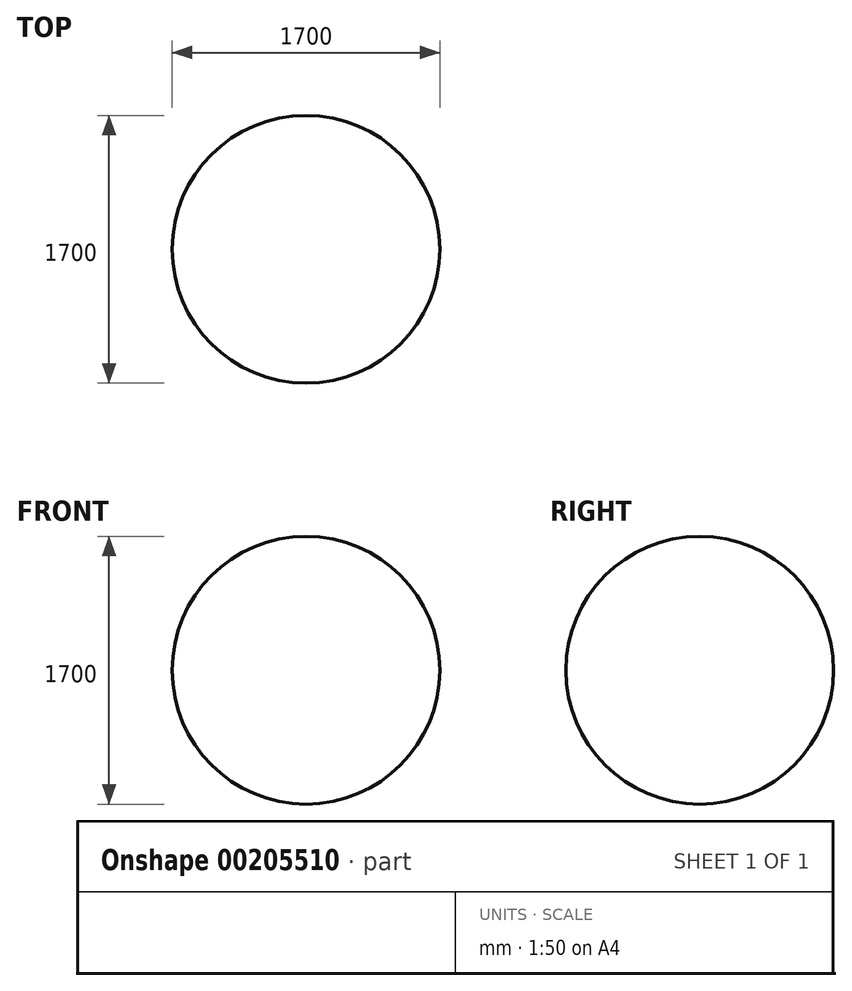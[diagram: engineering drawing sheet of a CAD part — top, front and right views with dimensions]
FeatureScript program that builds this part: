
annotation { "Feature Type Name" : "Feature", "Feature Type Description" : "" }
export const myFeature = defineFeature(function(context is Context, id is Id, definition is map)
    precondition{}
    {
        {
            var Q0;
            Q0=qCreatedBy(makeId("Front.planeOp"),FACE);
            var sketch = newSketch(context, id + "F0", { "sketchPlane" : qUnion([Q0])});
            skLineSegment(sketch, "E0", {"start": v(0, 0) * mm, "end": v(0, 850) * mm});
            skLineSegment(sketch, "E1", {"start": v(0, 0) * mm, "end": v(0, -850) * mm});
            skArc(sketch, "E2", {"start": v(0, 850) * mm, "mid": v(850, 0) * mm, "end": v(0, -850) * mm});
            skSolve(sketch);
        }
        {
            var Q0;
            Q0 = qSketchRegion(id + "F0", true);
            var Q1;
            Q1=sQuery(id+"F0.wireOp",EDGE,"E0");
            revolve(context, id + "F1", {"entities" : qUnion([Q0]), "axis" : qUnion([Q1]), "revolveType" : RevolveType.FULL});
        }
    });
